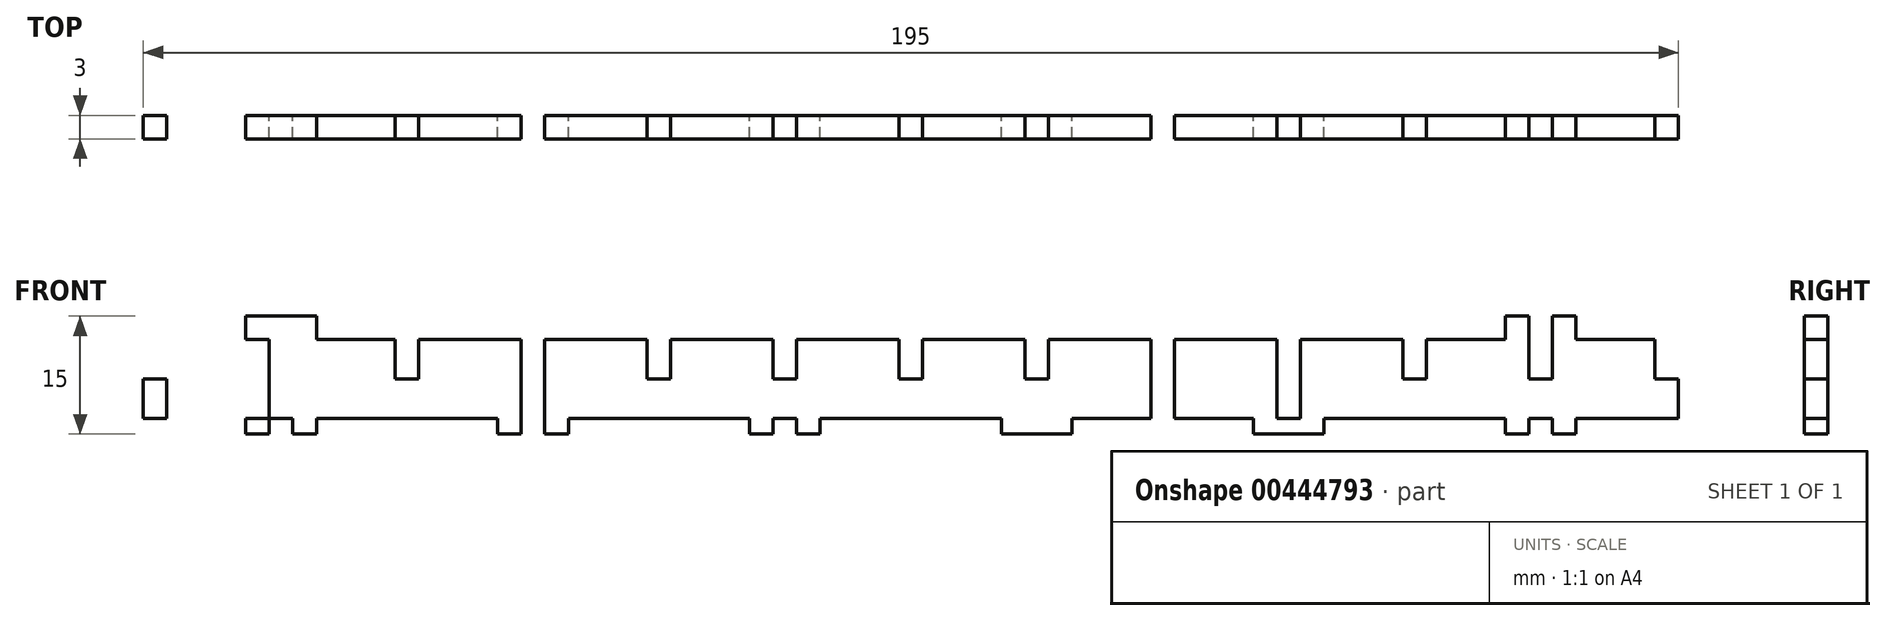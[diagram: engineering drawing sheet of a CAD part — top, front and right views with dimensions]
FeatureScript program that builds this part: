
annotation { "Feature Type Name" : "Feature", "Feature Type Description" : "" }
export const myFeature = defineFeature(function(context is Context, id is Id, definition is map)
    precondition{}
    {
        {
            var Q0;
            Q0=qCreatedBy(makeId("Front.planeOp"),FACE);
            var sketch = newSketch(context, id + "F0", { "sketchPlane" : qUnion([Q0])});
            skLineSegment(sketch, "E0", {"start": v(0, 0) * mm, "end": v(11.5, 0) * mm});
            skLineSegment(sketch, "E1", {"start": v(11.5, 0) * mm, "end": v(11.5, -2) * mm});
            skLineSegment(sketch, "E2", {"start": v(11.5, -2) * mm, "end": v(20.5, -2) * mm});
            skLineSegment(sketch, "E3", {"start": v(20.5, -2) * mm, "end": v(20.5, 0) * mm});
            skLineSegment(sketch, "E4", {"start": v(20.5, 0) * mm, "end": v(43.5, 0) * mm});
            skLineSegment(sketch, "E5", {"start": v(43.5, 0) * mm, "end": v(43.5, -2) * mm});
            skLineSegment(sketch, "E6", {"start": v(43.5, -2) * mm, "end": v(52.5, -2) * mm});
            skLineSegment(sketch, "E7", {"start": v(52.5, -2) * mm, "end": v(52.5, 0) * mm});
            skLineSegment(sketch, "E8", {"start": v(0, 0) * mm, "end": v(0, 10) * mm});
            skPoint(sketch, "E9.oppositeSnap0", {"position": v(0, 5) * mm});
            skLineSegment(sketch, "E9.bottom", {"start": v(0, 10) * mm, "end": v(-1.5, 10) * mm});
            skLineSegment(sketch, "E9.top", {"start": v(0, 5) * mm, "end": v(-1.5, 5) * mm});
            skLineSegment(sketch, "E9.left", {"start": v(0, 10) * mm, "end": v(0, 5) * mm});
            skLineSegment(sketch, "E9.right", {"start": v(-1.5, 10) * mm, "end": v(-1.5, 5) * mm});
            skLineSegment(sketch, "E10.bottom", {"start": v(14.5, 10) * mm, "end": v(17.5, 10) * mm});
            skLineSegment(sketch, "E10.top", {"start": v(14.5, 5) * mm, "end": v(17.5, 5) * mm});
            skLineSegment(sketch, "E10.left", {"start": v(14.5, 10) * mm, "end": v(14.5, 5) * mm});
            skLineSegment(sketch, "E10.right", {"start": v(17.5, 10) * mm, "end": v(17.5, 5) * mm});
            skLineSegment(sketch, "E11.top", {"start": v(0, 0) * mm, "end": v(-1.5, 0) * mm});
            skLineSegment(sketch, "E11.left", {"start": v(0, 5) * mm, "end": v(0, 0) * mm});
            skLineSegment(sketch, "E11.right", {"start": v(-1.5, 5) * mm, "end": v(-1.5, 0) * mm});
            skLineSegment(sketch, "E12.top", {"start": v(14.5, -2) * mm, "end": v(17.5, -2) * mm});
            skLineSegment(sketch, "E12.left", {"start": v(14.5, 5) * mm, "end": v(14.5, -2) * mm});
            skLineSegment(sketch, "E12.right", {"start": v(17.5, 5) * mm, "end": v(17.5, -2) * mm});
            skLineSegment(sketch, "E13.bottom", {"start": v(0, 10) * mm, "end": v(1.5, 10) * mm});
            skLineSegment(sketch, "E13.top", {"start": v(0, 5) * mm, "end": v(1.5, 5) * mm});
            skLineSegment(sketch, "E13.right", {"start": v(1.5, 10) * mm, "end": v(1.5, 5) * mm});
            skLineSegment(sketch, "E14.top", {"start": v(0, 0) * mm, "end": v(1.5, 0) * mm});
            skLineSegment(sketch, "E14.right", {"start": v(1.5, 5) * mm, "end": v(1.5, 0) * mm});
            skLineSegment(sketch, "E15.bottom", {"start": v(11.5, 10) * mm, "end": v(20.5, 10) * mm});
            skLineSegment(sketch, "E15.top", {"start": v(11.5, 13) * mm, "end": v(20.5, 13) * mm});
            skLineSegment(sketch, "E15.left", {"start": v(11.5, 10) * mm, "end": v(11.5, 13) * mm});
            skLineSegment(sketch, "E15.right", {"start": v(20.5, 10) * mm, "end": v(20.5, 13) * mm});
            skLineSegment(sketch, "E16", {"start": v(52.5, 0) * mm, "end": v(75.5, 0) * mm});
            skLineSegment(sketch, "E17", {"start": v(75.5, 0) * mm, "end": v(75.5, -2) * mm});
            skLineSegment(sketch, "E18", {"start": v(75.5, -2) * mm, "end": v(84.5, -2) * mm});
            skLineSegment(sketch, "E19", {"start": v(84.5, -2) * mm, "end": v(84.5, 0) * mm});
            skLineSegment(sketch, "E20", {"start": v(84.5, 0) * mm, "end": v(96, 0) * mm});
            skLineSegment(sketch, "E21", {"start": v(96, 0) * mm, "end": v(96, 19.13) * mm, "construction": true});
            skLineSegment(sketch, "E22", {"start": v(16, 10) * mm, "end": v(16, 11.65) * mm, "construction": true});
            skLineSegment(sketch, "E23.bottom", {"start": v(30.5, 0) * mm, "end": v(33.5, 0) * mm});
            skLineSegment(sketch, "E23.top", {"start": v(30.5, 5) * mm, "end": v(33.5, 5) * mm});
            skLineSegment(sketch, "E23.left", {"start": v(30.5, 0) * mm, "end": v(30.5, 5) * mm});
            skLineSegment(sketch, "E23.right", {"start": v(33.5, 0) * mm, "end": v(33.5, 5) * mm});
            skLineSegment(sketch, "E24.bottom", {"start": v(33.5, 5) * mm, "end": v(30.5, 5) * mm});
            skLineSegment(sketch, "E24.top", {"start": v(33.5, 10) * mm, "end": v(30.5, 10) * mm});
            skLineSegment(sketch, "E24.left", {"start": v(33.5, 5) * mm, "end": v(33.5, 10) * mm});
            skLineSegment(sketch, "E24.right", {"start": v(30.5, 5) * mm, "end": v(30.5, 10) * mm});
            skLineSegment(sketch, "E25", {"start": v(32, 0) * mm, "end": v(32, 2.31) * mm, "construction": true});
            skLineSegment(sketch, "E26.bottom", {"start": v(46.5, -2) * mm, "end": v(49.5, -2) * mm});
            skLineSegment(sketch, "E26.top", {"start": v(46.5, 5) * mm, "end": v(49.5, 5) * mm});
            skLineSegment(sketch, "E26.left", {"start": v(46.5, -2) * mm, "end": v(46.5, 5) * mm});
            skLineSegment(sketch, "E26.right", {"start": v(49.5, -2) * mm, "end": v(49.5, 5) * mm});
            skLineSegment(sketch, "E27.bottom", {"start": v(49.5, 5) * mm, "end": v(46.5, 5) * mm});
            skLineSegment(sketch, "E27.top", {"start": v(49.5, 10) * mm, "end": v(46.5, 10) * mm});
            skLineSegment(sketch, "E27.left", {"start": v(49.5, 5) * mm, "end": v(49.5, 10) * mm});
            skLineSegment(sketch, "E27.right", {"start": v(46.5, 5) * mm, "end": v(46.5, 10) * mm});
            skLineSegment(sketch, "E28.bottom", {"start": v(62.5, 0) * mm, "end": v(65.5, 0) * mm});
            skLineSegment(sketch, "E28.top", {"start": v(62.5, 5) * mm, "end": v(65.5, 5) * mm});
            skLineSegment(sketch, "E28.left", {"start": v(62.5, 0) * mm, "end": v(62.5, 5) * mm});
            skLineSegment(sketch, "E28.right", {"start": v(65.5, 0) * mm, "end": v(65.5, 5) * mm});
            skLineSegment(sketch, "E29.bottom", {"start": v(65.5, 5) * mm, "end": v(62.5, 5) * mm});
            skLineSegment(sketch, "E29.top", {"start": v(65.5, 10) * mm, "end": v(62.5, 10) * mm});
            skLineSegment(sketch, "E29.left", {"start": v(65.5, 5) * mm, "end": v(65.5, 10) * mm});
            skLineSegment(sketch, "E29.right", {"start": v(62.5, 5) * mm, "end": v(62.5, 10) * mm});
            skLineSegment(sketch, "E30.bottom", {"start": v(81.5, -2) * mm, "end": v(78.5, -2) * mm});
            skLineSegment(sketch, "E30.top", {"start": v(81.5, 5) * mm, "end": v(78.5, 5) * mm});
            skLineSegment(sketch, "E30.left", {"start": v(81.5, -2) * mm, "end": v(81.5, 5) * mm});
            skLineSegment(sketch, "E30.right", {"start": v(78.5, -2) * mm, "end": v(78.5, 5) * mm});
            skLineSegment(sketch, "E31.top", {"start": v(81.5, 10) * mm, "end": v(78.5, 10) * mm});
            skLineSegment(sketch, "E31.left", {"start": v(81.5, 5) * mm, "end": v(81.5, 10) * mm});
            skLineSegment(sketch, "E31.right", {"start": v(78.5, 5) * mm, "end": v(78.5, 10) * mm});
            skLineSegment(sketch, "E32.bottom", {"start": v(96, 0) * mm, "end": v(94.5, 0) * mm});
            skLineSegment(sketch, "E32.top", {"start": v(96, 5) * mm, "end": v(94.5, 5) * mm});
            skLineSegment(sketch, "E32.left", {"start": v(96, 0) * mm, "end": v(96, 5) * mm});
            skLineSegment(sketch, "E32.right", {"start": v(94.5, 0) * mm, "end": v(94.5, 5) * mm});
            skLineSegment(sketch, "E33.left", {"start": v(96, 5) * mm, "end": v(96, 5) * mm});
            skLineSegment(sketch, "E33.right", {"start": v(94.5, 5) * mm, "end": v(94.5, 5) * mm});
            skLineSegment(sketch, "E34.top", {"start": v(96, 10) * mm, "end": v(94.5, 10) * mm});
            skLineSegment(sketch, "E34.left", {"start": v(96, 5) * mm, "end": v(96, 10) * mm});
            skLineSegment(sketch, "E34.right", {"start": v(94.5, 5) * mm, "end": v(94.5, 10) * mm});
            skLineSegment(sketch, "E35", {"start": v(48, -2) * mm, "end": v(48, 0) * mm, "construction": true});
            skLineSegment(sketch, "E36", {"start": v(64, 0) * mm, "end": v(64, 2.67) * mm, "construction": true});
            skLineSegment(sketch, "E37", {"start": v(80, -2) * mm, "end": v(80, 0) * mm, "construction": true});
            skLineSegment(sketch, "E38", {"start": v(1.5, 10) * mm, "end": v(96, 10) * mm});
            skLineSegment(sketch, "E39.MirrorCS", {"start": v(96, 5) * mm, "end": v(97.5, 5) * mm});
            skLineSegment(sketch, "E40.MirrorCS", {"start": v(145.5, 5) * mm, "end": v(142.5, 5) * mm});
            skLineSegment(sketch, "E41.MirrorCS", {"start": v(110.5, 5) * mm, "end": v(113.5, 5) * mm});
            skLineSegment(sketch, "E42.MirrorCS", {"start": v(129.5, 5) * mm, "end": v(126.5, 5) * mm});
            skLineSegment(sketch, "E43.MirrorCS", {"start": v(177.5, 5) * mm, "end": v(174.5, 5) * mm});
            skLineSegment(sketch, "E44.MirrorCS", {"start": v(192, 5) * mm, "end": v(190.5, 5) * mm});
            skLineSegment(sketch, "E45.MirrorCS", {"start": v(192, 5) * mm, "end": v(193.5, 5) * mm});
            skLineSegment(sketch, "E46.MirrorCS", {"start": v(142.5, 5) * mm, "end": v(145.5, 5) * mm});
            skLineSegment(sketch, "E47.MirrorCS", {"start": v(126.5, 5) * mm, "end": v(129.5, 5) * mm});
            skLineSegment(sketch, "E48.MirrorCS", {"start": v(192, 10) * mm, "end": v(190.5, 10) * mm});
            skLineSegment(sketch, "E49.MirrorCS", {"start": v(171.5, -2) * mm, "end": v(171.5, 0) * mm});
            skLineSegment(sketch, "E50.MirrorCS", {"start": v(180.5, 0) * mm, "end": v(180.5, -2) * mm});
            skLineSegment(sketch, "E51.MirrorCS", {"start": v(177.5, 10) * mm, "end": v(174.5, 10) * mm});
            skLineSegment(sketch, "E52.MirrorCS", {"start": v(116.5, 0) * mm, "end": v(116.5, -2) * mm});
            skLineSegment(sketch, "E53.MirrorCS", {"start": v(177.5, -2) * mm, "end": v(174.5, -2) * mm});
            skLineSegment(sketch, "E54.MirrorCS", {"start": v(192, 0) * mm, "end": v(190.5, 0) * mm});
            skLineSegment(sketch, "E55.MirrorCS", {"start": v(126.5, 10) * mm, "end": v(129.5, 10) * mm});
            skLineSegment(sketch, "E56.MirrorCS", {"start": v(145.5, -2) * mm, "end": v(142.5, -2) * mm});
            skLineSegment(sketch, "E57.MirrorCS", {"start": v(110.5, -2) * mm, "end": v(113.5, -2) * mm});
            skLineSegment(sketch, "E58.MirrorCS", {"start": v(192, 0) * mm, "end": v(193.5, 0) * mm});
            skLineSegment(sketch, "E59.MirrorCS", {"start": v(96, 10) * mm, "end": v(97.5, 10) * mm});
            skLineSegment(sketch, "E60.MirrorCS", {"start": v(110.5, 10) * mm, "end": v(113.5, 10) * mm});
            skLineSegment(sketch, "E61.MirrorCS", {"start": v(142.5, 10) * mm, "end": v(145.5, 10) * mm});
            skLineSegment(sketch, "E62.MirrorCS", {"start": v(107.5, -2) * mm, "end": v(107.5, 0) * mm});
            skLineSegment(sketch, "E63.MirrorCS", {"start": v(192, 10) * mm, "end": v(193.5, 10) * mm});
            skLineSegment(sketch, "E64.MirrorCS", {"start": v(96, 0) * mm, "end": v(97.5, 0) * mm});
            skLineSegment(sketch, "E65.MirrorCS", {"start": v(139.5, -2) * mm, "end": v(139.5, 0) * mm});
            skLineSegment(sketch, "E66.MirrorCS", {"start": v(129.5, 0) * mm, "end": v(126.5, 0) * mm});
            skLineSegment(sketch, "E67.MirrorCS", {"start": v(148.5, 0) * mm, "end": v(148.5, -2) * mm});
            skLineSegment(sketch, "E68.MirrorCS", {"start": v(192, 5) * mm, "end": v(192, 0) * mm});
            skLineSegment(sketch, "E69.MirrorCS", {"start": v(112, -2) * mm, "end": v(112, 0) * mm, "construction": true});
            skLineSegment(sketch, "E70.MirrorCS", {"start": v(176, 10) * mm, "end": v(176, 11.65) * mm, "construction": true});
            skLineSegment(sketch, "E71.MirrorCS", {"start": v(192, 10) * mm, "end": v(192, 5) * mm});
            skLineSegment(sketch, "E72.MirrorCS", {"start": v(161.5, 0) * mm, "end": v(158.5, 0) * mm});
            skLineSegment(sketch, "E73.MirrorCS", {"start": v(128, 0) * mm, "end": v(128, 2.67) * mm, "construction": true});
            skLineSegment(sketch, "E74.MirrorCS", {"start": v(160, 0) * mm, "end": v(160, 2.31) * mm, "construction": true});
            skLineSegment(sketch, "E75.MirrorCS", {"start": v(144, -2) * mm, "end": v(144, 0) * mm, "construction": true});
            skLineSegment(sketch, "E76.MirrorCS", {"start": v(161.5, 5) * mm, "end": v(158.5, 5) * mm});
            skLineSegment(sketch, "E77.MirrorCS", {"start": v(171.5, 0) * mm, "end": v(148.5, 0) * mm});
            skLineSegment(sketch, "E78.MirrorCS", {"start": v(180.5, -2) * mm, "end": v(171.5, -2) * mm});
            skLineSegment(sketch, "E79.MirrorCS", {"start": v(192, 0) * mm, "end": v(180.5, 0) * mm});
            skLineSegment(sketch, "E80.MirrorCS", {"start": v(177.5, 10) * mm, "end": v(177.5, 5) * mm});
            skLineSegment(sketch, "E81.MirrorCS", {"start": v(158.5, 0) * mm, "end": v(158.5, 5) * mm});
            skLineSegment(sketch, "E82.MirrorCS", {"start": v(129.5, 0) * mm, "end": v(129.5, 5) * mm});
            skLineSegment(sketch, "E83.MirrorCS", {"start": v(97.5, 5) * mm, "end": v(97.5, 10) * mm});
            skPoint(sketch, "E84.MirrorP", {"position": v(192, 5) * mm});
            skLineSegment(sketch, "E85.MirrorCS", {"start": v(139.5, 0) * mm, "end": v(116.5, 0) * mm});
            skLineSegment(sketch, "E86.MirrorCS", {"start": v(126.5, 5) * mm, "end": v(126.5, 10) * mm});
            skLineSegment(sketch, "E87.MirrorCS", {"start": v(161.5, 5) * mm, "end": v(161.5, 10) * mm});
            skLineSegment(sketch, "E88.MirrorCS", {"start": v(180.5, 10) * mm, "end": v(180.5, 13) * mm});
            skLineSegment(sketch, "E89.MirrorCS", {"start": v(180.5, 13) * mm, "end": v(171.5, 13) * mm});
            skLineSegment(sketch, "E90.MirrorCS", {"start": v(158.5, 5) * mm, "end": v(158.5, 10) * mm});
            skLineSegment(sketch, "E91.MirrorCS", {"start": v(161.5, 0) * mm, "end": v(161.5, 5) * mm});
            skLineSegment(sketch, "E92.MirrorCS", {"start": v(107.5, 0) * mm, "end": v(96, 0) * mm});
            skLineSegment(sketch, "E93.MirrorCS", {"start": v(142.5, 5) * mm, "end": v(142.5, 10) * mm});
            skLineSegment(sketch, "E94.MirrorCS", {"start": v(193.5, 5) * mm, "end": v(193.5, 0) * mm});
            skLineSegment(sketch, "E95.MirrorCS", {"start": v(110.5, 5) * mm, "end": v(110.5, 10) * mm});
            skLineSegment(sketch, "E96.MirrorCS", {"start": v(180.5, 10) * mm, "end": v(171.5, 10) * mm});
            skLineSegment(sketch, "E97.MirrorCS", {"start": v(158.5, 10) * mm, "end": v(161.5, 10) * mm});
            skLineSegment(sketch, "E98.MirrorCS", {"start": v(145.5, 5) * mm, "end": v(145.5, 10) * mm});
            skLineSegment(sketch, "E99.MirrorCS", {"start": v(113.5, -2) * mm, "end": v(113.5, 5) * mm});
            skLineSegment(sketch, "E100.MirrorCS", {"start": v(174.5, 5) * mm, "end": v(174.5, -2) * mm});
            skLineSegment(sketch, "E101.MirrorCS", {"start": v(142.5, -2) * mm, "end": v(142.5, 5) * mm});
            skLineSegment(sketch, "E102.MirrorCS", {"start": v(113.5, 5) * mm, "end": v(113.5, 10) * mm});
            skLineSegment(sketch, "E103.MirrorCS", {"start": v(190.5, 10) * mm, "end": v(96, 10) * mm});
            skLineSegment(sketch, "E104.MirrorCS", {"start": v(190.5, 5) * mm, "end": v(190.5, 0) * mm});
            skLineSegment(sketch, "E105.MirrorCS", {"start": v(158.5, 5) * mm, "end": v(161.5, 5) * mm});
            skLineSegment(sketch, "E106.MirrorCS", {"start": v(126.5, 0) * mm, "end": v(126.5, 5) * mm});
            skLineSegment(sketch, "E107.MirrorCS", {"start": v(97.5, 0) * mm, "end": v(97.5, 5) * mm});
            skLineSegment(sketch, "E108.MirrorCS", {"start": v(174.5, 10) * mm, "end": v(174.5, 5) * mm});
            skLineSegment(sketch, "E109.MirrorCS", {"start": v(110.5, -2) * mm, "end": v(110.5, 5) * mm});
            skLineSegment(sketch, "E110.MirrorCS", {"start": v(177.5, 5) * mm, "end": v(177.5, -2) * mm});
            skLineSegment(sketch, "E111.MirrorCS", {"start": v(116.5, -2) * mm, "end": v(107.5, -2) * mm});
            skLineSegment(sketch, "E112.MirrorCS", {"start": v(145.5, -2) * mm, "end": v(145.5, 5) * mm});
            skLineSegment(sketch, "E113.MirrorCS", {"start": v(193.5, 10) * mm, "end": v(193.5, 5) * mm});
            skLineSegment(sketch, "E114.MirrorCS", {"start": v(129.5, 5) * mm, "end": v(129.5, 10) * mm});
            skLineSegment(sketch, "E115.MirrorCS", {"start": v(192, 0) * mm, "end": v(192, 10) * mm});
            skLineSegment(sketch, "E116.MirrorCS", {"start": v(148.5, -2) * mm, "end": v(139.5, -2) * mm});
            skLineSegment(sketch, "E117.MirrorCS", {"start": v(171.5, 10) * mm, "end": v(171.5, 13) * mm});
            skLineSegment(sketch, "E118.MirrorCS", {"start": v(190.5, 10) * mm, "end": v(190.5, 5) * mm});
            skLineSegment(sketch, "E119.top", {"start": v(14.5, 13) * mm, "end": v(17.5, 13) * mm});
            skLineSegment(sketch, "E119.left", {"start": v(14.5, 10) * mm, "end": v(14.5, 13) * mm});
            skLineSegment(sketch, "E119.right", {"start": v(17.5, 10) * mm, "end": v(17.5, 13) * mm});
            skLineSegment(sketch, "E120.bottom", {"start": v(174.5, 10) * mm, "end": v(177.5, 10) * mm});
            skLineSegment(sketch, "E120.top", {"start": v(174.5, 13) * mm, "end": v(177.5, 13) * mm});
            skLineSegment(sketch, "E120.left", {"start": v(174.5, 10) * mm, "end": v(174.5, 13) * mm});
            skLineSegment(sketch, "E120.right", {"start": v(177.5, 10) * mm, "end": v(177.5, 13) * mm});
            skLineSegment(sketch, "E121", {"start": v(11.5, 0) * mm, "end": v(180.5, 0) * mm});
            skSolve(sketch);
        }
        {
            var Q0;
            Q0=makeQuery(id+"F0.imprint","IMPRINT",FACE,{"disambiguationData":[TD([[makeQuery(id+"F0.imprint","IMPRINT",EDGE,{"derivedFrom":sQuery(id+"F0.wireOp",EDGE,"E0")}),1.0]])]});
            var Q1;
            Q1=makeQuery(id+"F0.imprint","IMPRINT",FACE,{"disambiguationData":[TD([[makeQuery(id+"F0.imprint","IMPRINT",EDGE,{"derivedFrom":sQuery(id+"F0.wireOp",EDGE,"E10.bottom")}),-1.0]])]});
            var Q2;
            {var subQ1=sQuery(id+"F0.wireOp",EDGE,"E10.right");Q2=makeQuery(id+"F0.imprint","IMPRINT",FACE,{"disambiguationData":[TD([[makeQuery(id+"F0.imprint","IMPRINT",EDGE,{"derivedFrom":subQ1}),1.0]])]});}
            var Q3;
            Q3=makeQuery(id+"F0.imprint","IMPRINT",FACE,{"disambiguationData":[TD([[makeQuery(id+"F0.imprint","IMPRINT",EDGE,{"derivedFrom":sQuery(id+"F0.wireOp",EDGE,"exBxU9Mq-clvg-588H-Zr5o-6X85DIsckNDc.bottom")}),1.0]])]});
            var Q4;
            {var subQ4=sQuery(id+"F0.wireOp",EDGE,"E5");Q4=makeQuery(id+"F0.imprint","IMPRINT",FACE,{"disambiguationData":[TD([[makeQuery(id+"F0.imprint","IMPRINT",EDGE,{"derivedFrom":subQ4}),1.0]])]});}
            var Q5;
            Q5=makeQuery(id+"F0.imprint","IMPRINT",FACE,{"disambiguationData":[TD([[makeQuery(id+"F0.imprint","IMPRINT",EDGE,{"derivedFrom":sQuery(id+"F0.wireOp",EDGE,"AYazpiCl-vhh2-3qVq-SwRU-viVl95edflrx.bottom")}),-1.0]])]});
            var Q6;
            {var subQ0=sQuery(id+"F0.wireOp",EDGE,"AYazpiCl-vhh2-3qVq-SwRU-viVl95edflrx.right");Q6=makeQuery(id+"F0.imprint","IMPRINT",FACE,{"disambiguationData":[TD([[makeQuery(id+"F0.imprint","IMPRINT",EDGE,{"derivedFrom":subQ0}),1.0]])]});}
            var Q7;
            Q7=makeQuery(id+"F0.imprint","IMPRINT",FACE,{"disambiguationData":[TD([[makeQuery(id+"F0.imprint","IMPRINT",EDGE,{"derivedFrom":sQuery(id+"F0.wireOp",EDGE,"4bEUlQAV-gPeH-rYiX-vIa2-gnOWGRHJXyY5.bottom")}),-1.0]])]});
            var Q8;
            Q8=makeQuery(id+"F0.imprint","IMPRINT",FACE,{"disambiguationData":[TD([[makeQuery(id+"F0.imprint","IMPRINT",EDGE,{"derivedFrom":sQuery(id+"F0.wireOp",EDGE,"73e3d719-c9b8-4955-bdff-4b6c16a5061d.1.0.2")}),1.0]])]});
            var Q9;
            Q9=makeQuery(id+"F0.imprint","IMPRINT",FACE,{"disambiguationData":[TD([[makeQuery(id+"F0.imprint","IMPRINT",EDGE,{"derivedFrom":sQuery(id+"F0.wireOp",EDGE,"RX1Oao4A-lbR6-l0fM-smuL-DuWmTi57Jbgw.bottom")}),-1.0]])]});
            var Q10;
            {var subQ2=sQuery(id+"F0.wireOp",EDGE,"RX1Oao4A-lbR6-l0fM-smuL-DuWmTi57Jbgw.right");Q10=makeQuery(id+"F0.imprint","IMPRINT",FACE,{"disambiguationData":[TD([[makeQuery(id+"F0.imprint","IMPRINT",EDGE,{"derivedFrom":subQ2}),1.0]])]});}
            var Q11;
            Q11=makeQuery(id+"F0.imprint","IMPRINT",FACE,{"disambiguationData":[TD([[makeQuery(id+"F0.imprint","IMPRINT",EDGE,{"derivedFrom":sQuery(id+"F0.wireOp",EDGE,"lx0Yxyhi-8TGn-ab6C-Jwk7-24dBiMFvEcRQ.bottom")}),1.0]])]});
            var Q12;
            Q12=makeQuery(id+"F0.imprint","IMPRINT",FACE,{"disambiguationData":[TD([[makeQuery(id+"F0.imprint","IMPRINT",EDGE,{"derivedFrom":sQuery(id+"F0.wireOp",EDGE,"73e3d719-c9b8-4955-bdff-4b6c16a5061d.2.0.2")}),1.0]])]});
            var Q13;
            Q13=makeQuery(id+"F0.imprint","IMPRINT",FACE,{"disambiguationData":[TD([[makeQuery(id+"F0.imprint","IMPRINT",EDGE,{"derivedFrom":sQuery(id+"F0.wireOp",EDGE,"l3f9ZwhA-5mlz-sbFQ-bDJ1-22Tfedz6XSHV.bottom")}),-1.0]])]});
            var Q14;
            {var subQ1=sQuery(id+"F0.wireOp",EDGE,"l3f9ZwhA-5mlz-sbFQ-bDJ1-22Tfedz6XSHV.right");Q14=makeQuery(id+"F0.imprint","IMPRINT",FACE,{"disambiguationData":[TD([[makeQuery(id+"F0.imprint","IMPRINT",EDGE,{"derivedFrom":subQ1}),1.0]])]});}
            var Q15;
            Q15=makeQuery(id+"F0.imprint","IMPRINT",FACE,{"disambiguationData":[TD([[makeQuery(id+"F0.imprint","IMPRINT",EDGE,{"derivedFrom":sQuery(id+"F0.wireOp",EDGE,"wGrJq75p-ImmZ-GG0w-oumq-Kc8NIA52VM4L.bottom")}),1.0]])]});
            var Q16;
            Q16=makeQuery(id+"F0.imprint","IMPRINT",FACE,{"disambiguationData":[TD([[makeQuery(id+"F0.imprint","IMPRINT",EDGE,{"derivedFrom":sQuery(id+"F0.wireOp",EDGE,"73e3d719-c9b8-4955-bdff-4b6c16a5061d.3.0.2")}),1.0]])]});
            var Q17;
            Q17=makeQuery(id+"F0.imprint","IMPRINT",FACE,{"disambiguationData":[TD([[makeQuery(id+"F0.imprint","IMPRINT",EDGE,{"derivedFrom":sQuery(id+"F0.wireOp",EDGE,"SeUBRtC9-CtK3-iZ4W-e8DI-C3XoFjQM9IDC.bottom")}),1.0]])]});
            var Q18;
            Q18=makeQuery(id+"F0.imprint","IMPRINT",FACE,{"disambiguationData":[TD([[makeQuery(id+"F0.imprint","IMPRINT",EDGE,{"derivedFrom":sQuery(id+"F0.wireOp",EDGE,"RVkCzXDl-vvve-KC9k-oys3-LpA8b4wrY5XK.bottom")}),-1.0]])]});
            var Q19;
            {var subQ0=sQuery(id+"F0.wireOp",EDGE,"wGrJq75p-ImmZ-GG0w-oumq-Kc8NIA52VM4L.left");Q19=makeQuery(id+"F0.imprint","IMPRINT",FACE,{"disambiguationData":[TD([[makeQuery(id+"F0.imprint","IMPRINT",EDGE,{"derivedFrom":subQ0}),-1.0]])]});}
            var Q20;
            Q20=makeQuery(id+"F0.imprint","IMPRINT",FACE,{"disambiguationData":[TD([[makeQuery(id+"F0.imprint","IMPRINT",EDGE,{"derivedFrom":sQuery(id+"F0.wireOp",EDGE,"E15.top")}),-1.0]])]});
            var Q21;
            {var subQ2=sQuery(id+"F0.wireOp",EDGE,"E7");Q21=makeQuery(id+"F0.imprint","IMPRINT",FACE,{"disambiguationData":[TD([[makeQuery(id+"F0.imprint","IMPRINT",EDGE,{"derivedFrom":subQ2}),1.0]])]});}
            var Q22;
            {var subQ1=sQuery(id+"F0.wireOp",EDGE,"E17");Q22=makeQuery(id+"F0.imprint","IMPRINT",FACE,{"disambiguationData":[TD([[makeQuery(id+"F0.imprint","IMPRINT",EDGE,{"derivedFrom":subQ1}),1.0]])]});}
            var Q23;
            {var subQ1=sQuery(id+"F0.wireOp",EDGE,"E19");Q23=makeQuery(id+"F0.imprint","IMPRINT",FACE,{"disambiguationData":[TD([[makeQuery(id+"F0.imprint","IMPRINT",EDGE,{"derivedFrom":subQ1}),1.0]])]});}
            var Q24;
            {var subQ2=sQuery(id+"F0.wireOp",EDGE,"E62.MirrorCS");Q24=makeQuery(id+"F0.imprint","IMPRINT",FACE,{"disambiguationData":[TD([[makeQuery(id+"F0.imprint","IMPRINT",EDGE,{"derivedFrom":subQ2}),-1.0]])]});}
            var Q25;
            {var subQ2=sQuery(id+"F0.wireOp",EDGE,"E52.MirrorCS");Q25=makeQuery(id+"F0.imprint","IMPRINT",FACE,{"disambiguationData":[TD([[makeQuery(id+"F0.imprint","IMPRINT",EDGE,{"derivedFrom":subQ2}),-1.0]])]});}
            var Q26;
            {var subQ2=sQuery(id+"F0.wireOp",EDGE,"E65.MirrorCS");Q26=makeQuery(id+"F0.imprint","IMPRINT",FACE,{"disambiguationData":[TD([[makeQuery(id+"F0.imprint","IMPRINT",EDGE,{"derivedFrom":subQ2}),-1.0]])]});}
            var Q27;
            {var subQ1=sQuery(id+"F0.wireOp",EDGE,"E67.MirrorCS");Q27=makeQuery(id+"F0.imprint","IMPRINT",FACE,{"disambiguationData":[TD([[makeQuery(id+"F0.imprint","IMPRINT",EDGE,{"derivedFrom":subQ1}),-1.0]])]});}
            var Q28;
            {var subQ2=sQuery(id+"F0.wireOp",EDGE,"E49.MirrorCS");Q28=makeQuery(id+"F0.imprint","IMPRINT",FACE,{"disambiguationData":[TD([[makeQuery(id+"F0.imprint","IMPRINT",EDGE,{"derivedFrom":subQ2}),-1.0]])]});}
            var Q29;
            {var subQ1=sQuery(id+"F0.wireOp",EDGE,"E50.MirrorCS");Q29=makeQuery(id+"F0.imprint","IMPRINT",FACE,{"disambiguationData":[TD([[makeQuery(id+"F0.imprint","IMPRINT",EDGE,{"derivedFrom":subQ1}),-1.0]])]});}
            var Q30;
            {var subQ3=sQuery(id+"F0.wireOp",EDGE,"E88.MirrorCS");Q30=makeQuery(id+"F0.imprint","IMPRINT",FACE,{"disambiguationData":[TD([[makeQuery(id+"F0.imprint","IMPRINT",EDGE,{"derivedFrom":subQ3}),1.0]])]});}
            var Q31;
            {var subQ0=sQuery(id+"F0.wireOp",EDGE,"E117.MirrorCS");Q31=makeQuery(id+"F0.imprint","IMPRINT",FACE,{"disambiguationData":[TD([[makeQuery(id+"F0.imprint","IMPRINT",EDGE,{"derivedFrom":subQ0}),-1.0]])]});}
            var Q32;
            {var subQ1=sQuery(id+"F0.wireOp",EDGE,"E23.right");Q32=makeQuery(id+"F0.imprint","IMPRINT",FACE,{"disambiguationData":[TD([[makeQuery(id+"F0.imprint","IMPRINT",EDGE,{"derivedFrom":subQ1}),-1.0]])]});}
            var Q33;
            {var subQ2=sQuery(id+"F0.wireOp",EDGE,"E27.left");Q33=makeQuery(id+"F0.imprint","IMPRINT",FACE,{"disambiguationData":[TD([[makeQuery(id+"F0.imprint","IMPRINT",EDGE,{"derivedFrom":subQ2}),-1.0]])]});}
            var Q34;
            {var subQ1=sQuery(id+"F0.wireOp",EDGE,"E28.right");Q34=makeQuery(id+"F0.imprint","IMPRINT",FACE,{"disambiguationData":[TD([[makeQuery(id+"F0.imprint","IMPRINT",EDGE,{"derivedFrom":subQ1}),-1.0]])]});}
            var Q35;
            {var subQ2=sQuery(id+"F0.wireOp",EDGE,"E31.left");Q35=makeQuery(id+"F0.imprint","IMPRINT",FACE,{"disambiguationData":[TD([[makeQuery(id+"F0.imprint","IMPRINT",EDGE,{"derivedFrom":subQ2}),-1.0]])]});}
            var Q36;
            {var subQ2=sQuery(id+"F0.wireOp",EDGE,"E83.MirrorCS");Q36=makeQuery(id+"F0.imprint","IMPRINT",FACE,{"disambiguationData":[TD([[makeQuery(id+"F0.imprint","IMPRINT",EDGE,{"derivedFrom":subQ2}),-1.0]])]});}
            var Q37;
            {var subQ1=sQuery(id+"F0.wireOp",EDGE,"E86.MirrorCS");Q37=makeQuery(id+"F0.imprint","IMPRINT",FACE,{"disambiguationData":[TD([[makeQuery(id+"F0.imprint","IMPRINT",EDGE,{"derivedFrom":subQ1}),1.0]])]});}
            var Q38;
            {var subQ6=sQuery(id+"F0.wireOp",EDGE,"E82.MirrorCS");Q38=makeQuery(id+"F0.imprint","IMPRINT",FACE,{"disambiguationData":[TD([[makeQuery(id+"F0.imprint","IMPRINT",EDGE,{"derivedFrom":subQ6}),-1.0]])]});}
            var Q39;
            {var subQ7=sQuery(id+"F0.wireOp",EDGE,"E81.MirrorCS");Q39=makeQuery(id+"F0.imprint","IMPRINT",FACE,{"disambiguationData":[TD([[makeQuery(id+"F0.imprint","IMPRINT",EDGE,{"derivedFrom":subQ7}),1.0]])]});}
            var Q40;
            {var subQ7=sQuery(id+"F0.wireOp",EDGE,"E87.MirrorCS");Q40=makeQuery(id+"F0.imprint","IMPRINT",FACE,{"disambiguationData":[TD([[makeQuery(id+"F0.imprint","IMPRINT",EDGE,{"derivedFrom":subQ7}),-1.0]])]});}
            var Q41;
            {var subQ1=sQuery(id+"F0.wireOp",EDGE,"E80.MirrorCS");Q41=makeQuery(id+"F0.imprint","IMPRINT",FACE,{"disambiguationData":[TD([[makeQuery(id+"F0.imprint","IMPRINT",EDGE,{"derivedFrom":subQ1}),1.0]])]});}
            var Q42;
            Q42=makeQuery(id+"F0.imprint","IMPRINT",FACE,{"disambiguationData":[TD([[makeQuery(id+"F0.imprint","IMPRINT",EDGE,{"derivedFrom":sQuery(id+"F0.wireOp",EDGE,"E13.top")}),-1.0]])]});
            var Q43;
            Q43=makeQuery(id+"F0.imprint","IMPRINT",FACE,{"disambiguationData":[TD([[makeQuery(id+"F0.imprint","IMPRINT",EDGE,{"derivedFrom":sQuery(id+"F0.wireOp",EDGE,"E9.top")}),1.0]])]});
            var Q44;
            {var subQ0=sQuery(id+"F0.wireOp",EDGE,"E12.top");Q44=makeQuery(id+"F0.imprint","IMPRINT",FACE,{"disambiguationData":[TD([[makeQuery(id+"F0.imprint","IMPRINT",EDGE,{"derivedFrom":subQ0}),1.0]])]});}
            var Q45;
            {var subQ0=sQuery(id+"F0.wireOp",EDGE,"E10.top");Q45=makeQuery(id+"F0.imprint","IMPRINT",FACE,{"disambiguationData":[TD([[makeQuery(id+"F0.imprint","IMPRINT",EDGE,{"derivedFrom":subQ0}),-1.0]])]});}
            var Q46;
            {var subQ0=sQuery(id+"F0.wireOp",EDGE,"E23.left");Q46=makeQuery(id+"F0.imprint","IMPRINT",FACE,{"disambiguationData":[TD([[makeQuery(id+"F0.imprint","IMPRINT",EDGE,{"derivedFrom":subQ0}),-1.0]])]});}
            var Q47;
            {var subQ0=sQuery(id+"F0.wireOp",EDGE,"E26.bottom");Q47=makeQuery(id+"F0.imprint","IMPRINT",FACE,{"disambiguationData":[TD([[makeQuery(id+"F0.imprint","IMPRINT",EDGE,{"derivedFrom":subQ0}),1.0]])]});}
            var Q48;
            {var subQ0=sQuery(id+"F0.wireOp",EDGE,"E27.bottom");Q48=makeQuery(id+"F0.imprint","IMPRINT",FACE,{"disambiguationData":[TD([[makeQuery(id+"F0.imprint","IMPRINT",EDGE,{"derivedFrom":subQ0}),1.0]])]});}
            var Q49;
            {var subQ0=sQuery(id+"F0.wireOp",EDGE,"E1");Q49=makeQuery(id+"F0.imprint","IMPRINT",FACE,{"disambiguationData":[TD([[makeQuery(id+"F0.imprint","IMPRINT",EDGE,{"derivedFrom":subQ0}),1.0]])]});}
            var Q50;
            {var subQ0=sQuery(id+"F0.wireOp",EDGE,"E3");Q50=makeQuery(id+"F0.imprint","IMPRINT",FACE,{"disambiguationData":[TD([[makeQuery(id+"F0.imprint","IMPRINT",EDGE,{"derivedFrom":subQ0}),1.0]])]});}
            var Q51;
            {var subQ0=sQuery(id+"F0.wireOp",EDGE,"E28.left");Q51=makeQuery(id+"F0.imprint","IMPRINT",FACE,{"disambiguationData":[TD([[makeQuery(id+"F0.imprint","IMPRINT",EDGE,{"derivedFrom":subQ0}),-1.0]])]});}
            var Q52;
            {var subQ0=sQuery(id+"F0.wireOp",EDGE,"E30.top");Q52=makeQuery(id+"F0.imprint","IMPRINT",FACE,{"disambiguationData":[TD([[makeQuery(id+"F0.imprint","IMPRINT",EDGE,{"derivedFrom":subQ0}),1.0]])]});}
            var Q53;
            {var subQ0=sQuery(id+"F0.wireOp",EDGE,"E30.bottom");Q53=makeQuery(id+"F0.imprint","IMPRINT",FACE,{"disambiguationData":[TD([[makeQuery(id+"F0.imprint","IMPRINT",EDGE,{"derivedFrom":subQ0}),-1.0]])]});}
            var Q54;
            Q54=makeQuery(id+"F0.imprint","IMPRINT",FACE,{"disambiguationData":[TD([[makeQuery(id+"F0.imprint","IMPRINT",EDGE,{"derivedFrom":sQuery(id+"F0.wireOp",EDGE,"E39.MirrorCS")}),-1.0]])]});
            var Q55;
            {var subQ0=sQuery(id+"F0.wireOp",EDGE,"E41.MirrorCS");Q55=makeQuery(id+"F0.imprint","IMPRINT",FACE,{"disambiguationData":[TD([[makeQuery(id+"F0.imprint","IMPRINT",EDGE,{"derivedFrom":subQ0}),-1.0]])]});}
            var Q56;
            {var subQ0=sQuery(id+"F0.wireOp",EDGE,"E111.MirrorCS");var subQ1=sQuery(id+"F0.wireOp",EDGE,"E99.MirrorCS");var subQ2=makeQuery(id+"F0.imprint","INTERSECT",VERTEX,{"derivedFrom":[subQ1,subQ0]});Q56=makeQuery(id+"F0.imprint","IMPRINT",FACE,{"disambiguationData":[TD([[makeQuery(id+"F0.imprint","IMPRINT",EDGE,{"disambiguationData":[TD([[subQ2,-1.0]])],"derivedFrom":subQ1}),1.0]])]});}
            var Q57;
            Q57=makeQuery(id+"F0.imprint","IMPRINT",FACE,{"disambiguationData":[TD([[makeQuery(id+"F0.imprint","IMPRINT",EDGE,{"derivedFrom":sQuery(id+"F0.wireOp",EDGE,"E47.MirrorCS")}),-1.0]])]});
            var Q58;
            {var subQ0=sQuery(id+"F0.wireOp",EDGE,"E46.MirrorCS");Q58=makeQuery(id+"F0.imprint","IMPRINT",FACE,{"disambiguationData":[TD([[makeQuery(id+"F0.imprint","IMPRINT",EDGE,{"derivedFrom":subQ0}),-1.0]])]});}
            var Q59;
            {var subQ0=sQuery(id+"F0.wireOp",EDGE,"E116.MirrorCS");var subQ1=sQuery(id+"F0.wireOp",EDGE,"E101.MirrorCS");var subQ2=makeQuery(id+"F0.imprint","INTERSECT",VERTEX,{"derivedFrom":[subQ1,subQ0]});Q59=makeQuery(id+"F0.imprint","IMPRINT",FACE,{"disambiguationData":[TD([[makeQuery(id+"F0.imprint","IMPRINT",EDGE,{"disambiguationData":[TD([[subQ2,-1.0]])],"derivedFrom":subQ1}),-1.0]])]});}
            var Q60;
            {var subQ0=sQuery(id+"F0.wireOp",EDGE,"E81.MirrorCS");Q60=makeQuery(id+"F0.imprint","IMPRINT",FACE,{"disambiguationData":[TD([[makeQuery(id+"F0.imprint","IMPRINT",EDGE,{"derivedFrom":subQ0}),-1.0]])]});}
            var Q61;
            {var subQ0=sQuery(id+"F0.wireOp",EDGE,"E32.right");Q61=makeQuery(id+"F0.imprint","IMPRINT",FACE,{"disambiguationData":[TD([[makeQuery(id+"F0.imprint","IMPRINT",EDGE,{"derivedFrom":subQ0}),-1.0]])]});}
            var Q62;
            {var subQ0=sQuery(id+"F0.wireOp",EDGE,"E43.MirrorCS");Q62=makeQuery(id+"F0.imprint","IMPRINT",FACE,{"disambiguationData":[TD([[makeQuery(id+"F0.imprint","IMPRINT",EDGE,{"derivedFrom":subQ0}),1.0]])]});}
            var Q63;
            {var subQ0=sQuery(id+"F0.wireOp",EDGE,"E100.MirrorCS");var subQ1=sQuery(id+"F0.wireOp",EDGE,"E78.MirrorCS");var subQ2=makeQuery(id+"F0.imprint","INTERSECT",VERTEX,{"derivedFrom":[subQ1,subQ0]});Q63=makeQuery(id+"F0.imprint","IMPRINT",FACE,{"disambiguationData":[TD([[makeQuery(id+"F0.imprint","IMPRINT",EDGE,{"disambiguationData":[TD([[subQ2,1.0]])],"derivedFrom":subQ1}),-1.0]])]});}
            var Q64;
            {var subQ0=sQuery(id+"F0.wireOp",EDGE,"E44.MirrorCS");Q64=makeQuery(id+"F0.imprint","IMPRINT",FACE,{"disambiguationData":[TD([[makeQuery(id+"F0.imprint","IMPRINT",EDGE,{"derivedFrom":subQ0}),1.0]])]});}
            var Q65;
            {var subQ0=sQuery(id+"F0.wireOp",EDGE,"E45.MirrorCS");Q65=makeQuery(id+"F0.imprint","IMPRINT",FACE,{"disambiguationData":[TD([[makeQuery(id+"F0.imprint","IMPRINT",EDGE,{"derivedFrom":subQ0}),-1.0]])]});}
            extrude(context, id + "F1", {"entities" : qUnion([Q0, Q1, Q2, Q3, Q4, Q5, Q6, Q7, Q8, Q9, Q10, Q11, Q12, Q13, Q14, Q15, Q16, Q17, Q18, Q19, Q20, Q21, Q22, Q23, Q24, Q25, Q26, Q27, Q28, Q29, Q30, Q31, Q32, Q33, Q34, Q35, Q36, Q37, Q38, Q39, Q40, Q41, Q42, Q43, Q44, Q45, Q46, Q47, Q48, Q49, Q50, Q51, Q52, Q53, Q54, Q55, Q56, Q57, Q58, Q59, Q60, Q61, Q62, Q63, Q64, Q65]), "depth" : 3 * mm});
        }
    });
